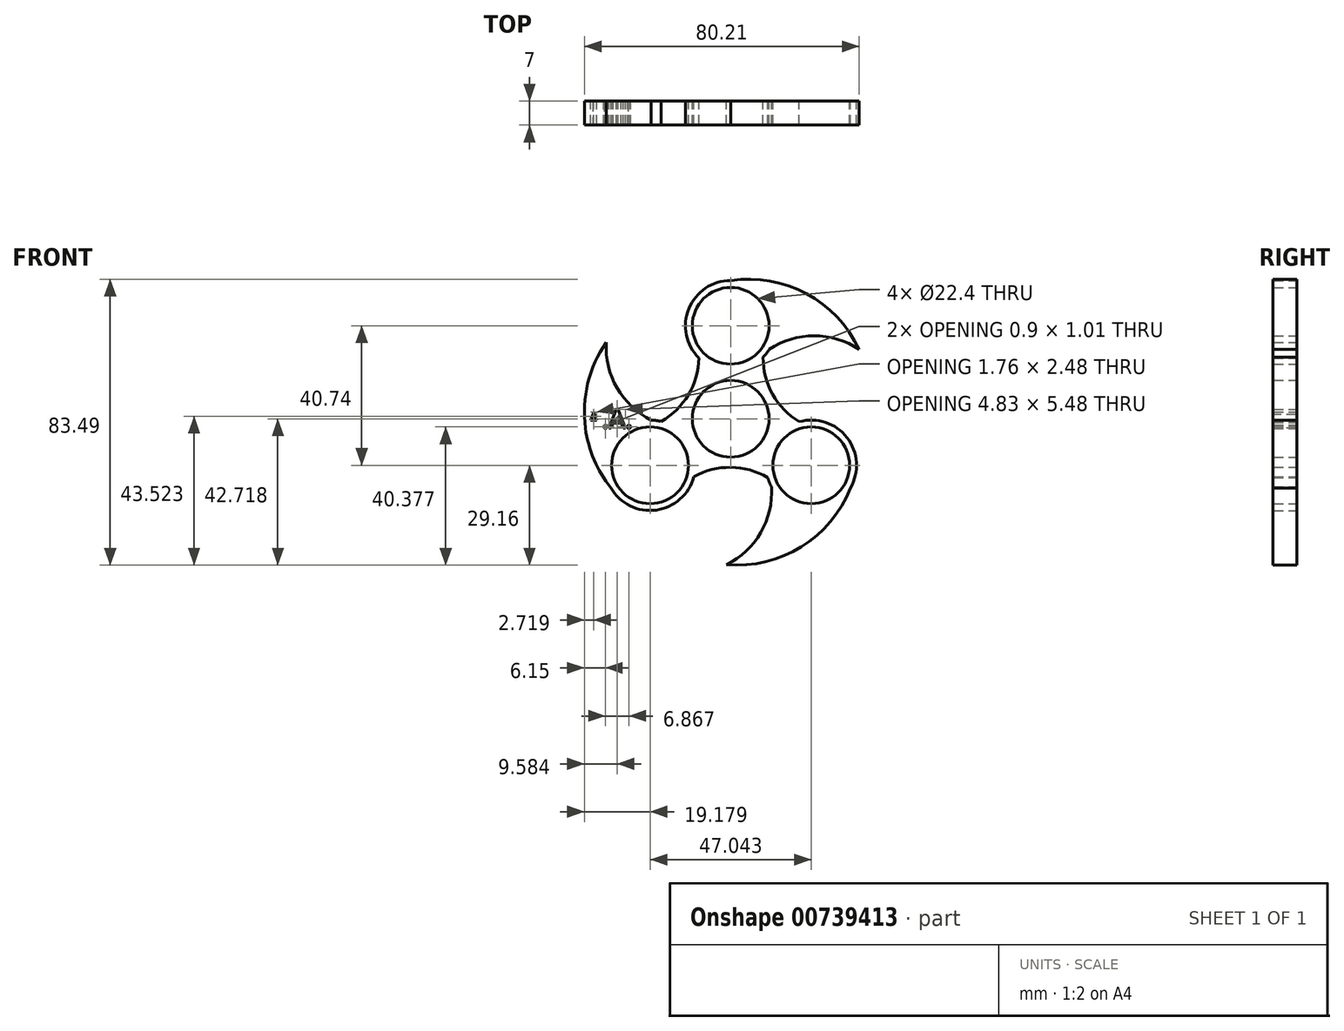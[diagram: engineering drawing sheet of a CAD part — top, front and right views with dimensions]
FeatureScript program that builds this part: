
annotation { "Feature Type Name" : "Feature", "Feature Type Description" : "" }
export const myFeature = defineFeature(function(context is Context, id is Id, definition is map)
    precondition{}
    {
        {
            var Q0;
            Q0=qCreatedBy(makeId("Front.planeOp"),FACE);
            var sketch = newSketch(context, id + "F0", { "sketchPlane" : qUnion([Q0])});
            skCircle(sketch, "E0", {"center": v(0, 0) * mm, "radius": 11.2 * mm});
            skCircle(sketch, "E1", {"center": v(0, 27.16) * mm, "radius": 11.2 * mm});
            skArc(sketch, "E2", {"start": v(9.45, 17.95) * mm, "mid": v(10.42, 19.05) * mm, "end": v(11.25, 20.26) * mm});
            skArc(sketch, "E3.1.0", {"start": v(-34.95, -20.18) * mm, "mid": v(-21.76, -26.66) * mm, "end": v(-10.75, -16.92) * mm});
            skCircle(sketch, "E3.1.1", {"center": v(-23.52, -13.58) * mm, "radius": 11.2 * mm});
            skArc(sketch, "E3.2.0", {"start": v(10.82, -17.16) * mm, "mid": v(11.3, -18.55) * mm, "end": v(11.92, -19.88) * mm});
            skArc(sketch, "E4", {"start": v(37.5, 20.26) * mm, "mid": v(22.09, 36.53) * mm, "end": v(0, 40.36) * mm});
            skArc(sketch, "E5", {"start": v(37.5, 20.26) * mm, "mid": v(24.38, 24.22) * mm, "end": v(11.25, 20.26) * mm});
            skArc(sketch, "E6.1.0", {"start": v(-36.3, 22.35) * mm, "mid": v(-33.16, 9) * mm, "end": v(-23.17, -0.38) * mm});
            skArc(sketch, "E6.1.1", {"start": v(-36.3, 22.35) * mm, "mid": v(-42.68, 0.86) * mm, "end": v(-34.95, -20.18) * mm});
            skArc(sketch, "E6.2.0", {"start": v(-1.2, -42.61) * mm, "mid": v(8.78, -33.22) * mm, "end": v(11.92, -19.88) * mm});
            skArc(sketch, "E6.2.1", {"start": v(-1.2, -42.61) * mm, "mid": v(20.6, -37.4) * mm, "end": v(34.95, -20.18) * mm});
            skPoint(sketch, "E7.end.orphan", {"position": v(-9.27, 20.88) * mm});
            skArc(sketch, "E8", {"start": v(-20.27, -0.79) * mm, "mid": v(-12.32, 7.04) * mm, "end": v(-9.27, 17.77) * mm});
            skArc(sketch, "E9.1.0", {"start": v(10.82, -17.16) * mm, "mid": v(0.07, -14.18) * mm, "end": v(-10.75, -16.92) * mm});
            skArc(sketch, "E9.2.0", {"start": v(9.45, 17.95) * mm, "mid": v(12.25, 7.15) * mm, "end": v(20.02, -0.85) * mm});
            skArc(sketch, "E10.trimOffspring", {"start": v(0, 40.36) * mm, "mid": v(-12.21, 32.17) * mm, "end": v(-9.27, 17.77) * mm});
            skCircle(sketch, "E11", {"center": v(23.52, -13.58) * mm, "radius": 11.2 * mm});
            skArc(sketch, "E12.trimOffspring", {"start": v(-20.27, -0.79) * mm, "mid": v(-21.71, -0.5) * mm, "end": v(-23.17, -0.38) * mm});
            skArc(sketch, "E13.trimOffspring", {"start": v(34.95, -20.18) * mm, "mid": v(33.97, -5.51) * mm, "end": v(20.02, -0.85) * mm});
            skText(sketch, "E14", { "text": "A.A.", "fontName": "OpenSans-Regular.ttf"});
            const initialGuessF0  = {"E14": [-0.0424, -0.00276, 1, 0, 0.0055]};
            skSetInitialGuess(sketch, initialGuessF0);
            skSolve(sketch);
        }
        {
            var Q0;
            Q0 = qSketchRegion(id + "F0", true);
            extrude(context, id + "F1", {"entities" : qUnion([Q0]), "depth" : 7 * mm, "offsetDistance" : 25 * mm});
        }
    });
